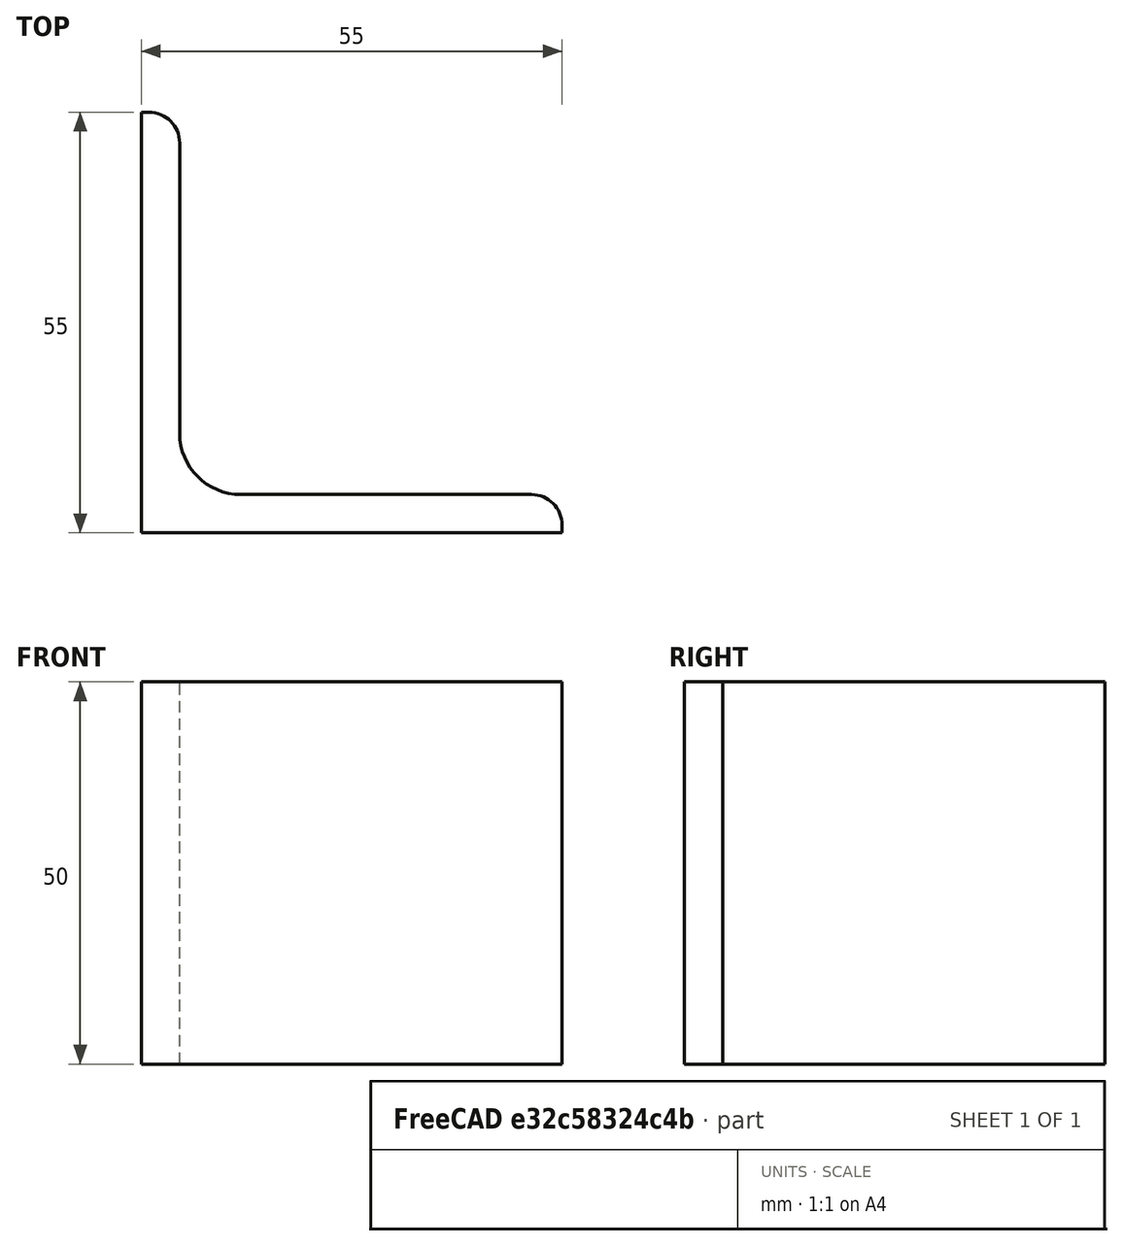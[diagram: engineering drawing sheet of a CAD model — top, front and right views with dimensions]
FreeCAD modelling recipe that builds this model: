
FCSTD DOCUMENT  (FreeCAD 0.15R4671 (Git))
Label: Angle Bar L55x55x5 EN10056 S235JR
License: All rights reserved
LicenseURL: http://en.wikipedia.org/wiki/All_rights_reserved
objects: Sketcher::SketchObject×1, Part::Extrusion×1
note: 2 computed .brp shape members not serialized (recipe doc carries the construction recipe); baked Part::Feature solids carry a one-line shape summary decoded from their .brp

FEATURE [Sketcher::SketchObject] Sketch
  sketch-geometry (9):
    g0: LineSegment StartX=0 StartY=0 StartZ=0 EndX=55 EndY=0 EndZ=0
    g1: LineSegment StartX=55 StartY=0 StartZ=0 EndX=55 EndY=1 EndZ=0
    g2: LineSegment StartX=51 StartY=5 StartZ=0 EndX=13 EndY=5 EndZ=0
    g3: LineSegment StartX=0 StartY=0 StartZ=0 EndX=0 EndY=55 EndZ=0
    g4: LineSegment StartX=0 StartY=55 StartZ=0 EndX=1 EndY=55 EndZ=0
    g5: LineSegment StartX=5 StartY=51 StartZ=0 EndX=5 EndY=13 EndZ=0
    g6: ArcOfCircle CenterX=13 CenterY=13 CenterZ=0 NormalX=0 NormalY=0 NormalZ=1 Radius=8 StartAngle=3.14159 EndAngle=4.71239
    g7: ArcOfCircle CenterX=1 CenterY=51 CenterZ=0 NormalX=0 NormalY=0 NormalZ=1 Radius=4 StartAngle=0 EndAngle=1.5708
    g8: ArcOfCircle CenterX=51 CenterY=1 CenterZ=0 NormalX=0 NormalY=0 NormalZ=1 Radius=4 StartAngle=0 EndAngle=1.5708
  constraints (23):
    c: Coincident(g0,g-1)
    c: Horizontal(g0)
    c: Coincident(g1,g0)
    c: Vertical(g1)
    c: Horizontal(g2)
    c: Coincident(g3,g-1)
    c: Vertical(g3)
    c: Coincident(g4,g3)
    c: Horizontal(g4)
    c: Vertical(g5)
    c: Tangent(g5,g6) = -1.5708
    c: Tangent(g2,g6) = 1.5708
    c: Tangent(g4,g7) = 1.5708
    c: Tangent(g5,g7) = 1.5708
    c: Tangent(g2,g8) = -1.5708
    c: Tangent(g1,g8) = -1.5708
    c: DistanceX(g0) = 55
    c: DistanceY(g3) = 55
    c: DistanceY(g0,g2) = 5
    c: DistanceX(g3,g5) = 5
    c: Radius(g6) = 8
    c: Radius(g8) = 4
    c: Radius(g7) = 4
FEATURE [Part::Extrusion] Extrude  label="Angle Bar L55x55x5 EN10056 S235JR"
  Base = -> Sketch
  Dir = (0,0,50)
  Solid = true
